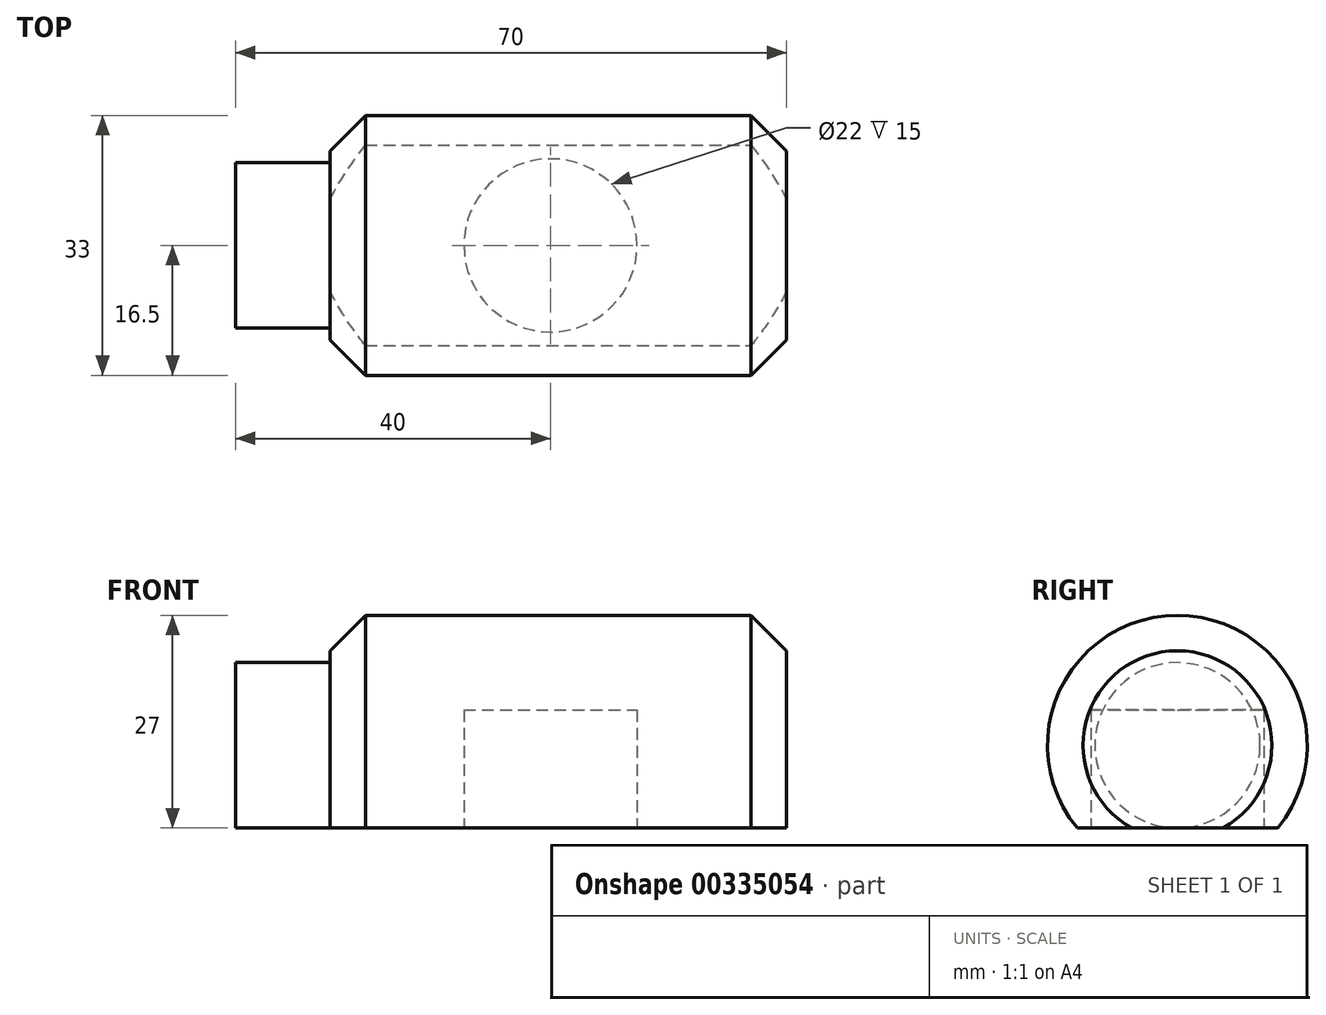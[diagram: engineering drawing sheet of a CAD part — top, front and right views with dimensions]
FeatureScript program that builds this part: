
annotation { "Feature Type Name" : "Feature", "Feature Type Description" : "" }
export const myFeature = defineFeature(function(context is Context, id is Id, definition is map)
    precondition{}
    {
        {
            var Q0;
            Q0=qCreatedBy(makeId("Front.planeOp"),FACE);
            var sketch = newSketch(context, id + "F0", { "sketchPlane" : qUnion([Q0])});
            skLineSegment(sketch, "E0", {"start": v(0, 0) * mm, "end": v(0, 10.5) * mm});
            skLineSegment(sketch, "E1", {"start": v(0, 10.5) * mm, "end": v(12, 10.5) * mm});
            skLineSegment(sketch, "E2", {"start": v(16.5, 16.5) * mm, "end": v(65.5, 16.5) * mm});
            skLineSegment(sketch, "E3", {"start": v(65.5, 16.5) * mm, "end": v(70, 12) * mm});
            skLineSegment(sketch, "E4", {"start": v(70, 12) * mm, "end": v(70, 0) * mm});
            skLineSegment(sketch, "E5", {"start": v(70, 0) * mm, "end": v(0, 0) * mm});
            skLineSegment(sketch, "E6", {"start": v(0, 0) * mm, "end": v(-15.16, 0) * mm, "construction": true});
            skLineSegment(sketch, "E7", {"start": v(12, 10.5) * mm, "end": v(12, 12) * mm});
            skLineSegment(sketch, "E8", {"start": v(12, 12) * mm, "end": v(16.5, 16.5) * mm});
            skSolve(sketch);
        }
        {
            var Q0;
            Q0=makeQuery(id+"F0.imprint","IMPRINT",FACE,{"disambiguationData":[TD([[makeQuery(id+"F0.imprint","IMPRINT",EDGE,{"derivedFrom":sQuery(id+"F0.wireOp",EDGE,"E0")}),-1.0]])]});
            var Q1;
            Q1=sQuery(id+"F0.wireOp",EDGE,"E6");
            revolve(context, id + "F1", {"entities" : qUnion([Q0]), "axis" : qUnion([Q1]), "revolveType" : RevolveType.FULL});
        }
        {
            var Q0;
            Q0=makeQuery(id+"F1.opRevolve","SWEPT_FACE",FACE,{"disambiguationData":[OSD([sQuery(id+"F0.wireOp",EDGE,"E4")])]});
            var sketch = newSketch(context, id + "F2", { "sketchPlane" : qUnion([Q0])});
            skLineSegment(sketch, "E9", {"start": v(-12.73, -10.5) * mm, "end": v(12.73, -10.5) * mm});
            skCircle(sketch, "E10.0", {"center": v(0, 0) * mm, "radius": 16.5 * mm});
            skSolve(sketch);
        }
        {
            var Q0;
            {var subQ0=sQuery(id+"F2.wireOp",EDGE,"E10.0");var subQ1=sQuery(id+"F2.wireOp",EDGE,"E9");var subQ2=makeQuery(id+"F2.imprint","INTERSECT",VERTEX,{"disambiguationData":[OD(0.0)],"derivedFrom":[subQ1,subQ0]});Q0=makeQuery(id+"F2.imprint","IMPRINT",FACE,{"disambiguationData":[TD([[makeQuery(id+"F2.imprint","IMPRINT",EDGE,{"disambiguationData":[TD([[subQ2,-1.0]])],"derivedFrom":subQ0}),1.0]])]});}
            var Q1;
            {var subQ0=sQuery(id+"F2.wireOp",EDGE,"E9");var subQ1=makeQuery(id+"F1.opRevolve","SWEPT_EDGE",EDGE,{"disambiguationData":[OSD([sQuery(id+"F0.wireOp",EDGE,"E3"),sQuery(id+"F0.wireOp",EDGE,"E4")])]});var subQ2=makeQuery(id+"F2.imprint","INTERSECT",VERTEX,{"disambiguationData":[OD(0.0)],"derivedFrom":[subQ1,subQ0]});Q1=makeQuery(id+"F2.imprint","IMPRINT",FACE,{"disambiguationData":[TD([[makeQuery(id+"F2.imprint","IMPRINT",EDGE,{"disambiguationData":[TD([[subQ2,-1.0]])],"derivedFrom":subQ0}),-1.0]])]});}
            extrude(context, id + "F3", {"entities" : qUnion([Q0, Q1]), "operationType" : NewBodyOperationType.REMOVE, "oppositeDirection" : true, "depth" : 73.8 * mm});
        }
        {
            var Q0;
            Q0=makeQuery(id+"F3.boolean.opBoolean","COPY",FACE,{"derivedFrom":makeQuery(id+"F3.opExtrude","SWEPT_FACE",FACE,{"disambiguationData":[OSD([sQuery(id+"F2.wireOp",EDGE,"E9")])]})});
            var sketch = newSketch(context, id + "F4", { "sketchPlane" : qUnion([Q0])});
            skCircle(sketch, "E11", {"center": v(40, 0) * mm, "radius": 11 * mm});
            skSolve(sketch);
        }
        {
            var Q0;
            Q0=makeQuery(id+"F4.imprint","IMPRINT",FACE,{"disambiguationData":[TD([[makeQuery(id+"F4.imprint","IMPRINT",EDGE,{"derivedFrom":sQuery(id+"F4.wireOp",EDGE,"E11")}),1.0]])]});
            extrude(context, id + "F5", {"entities" : qUnion([Q0]), "operationType" : NewBodyOperationType.REMOVE, "oppositeDirection" : true, "depth" : 15 * mm});
        }
    });
